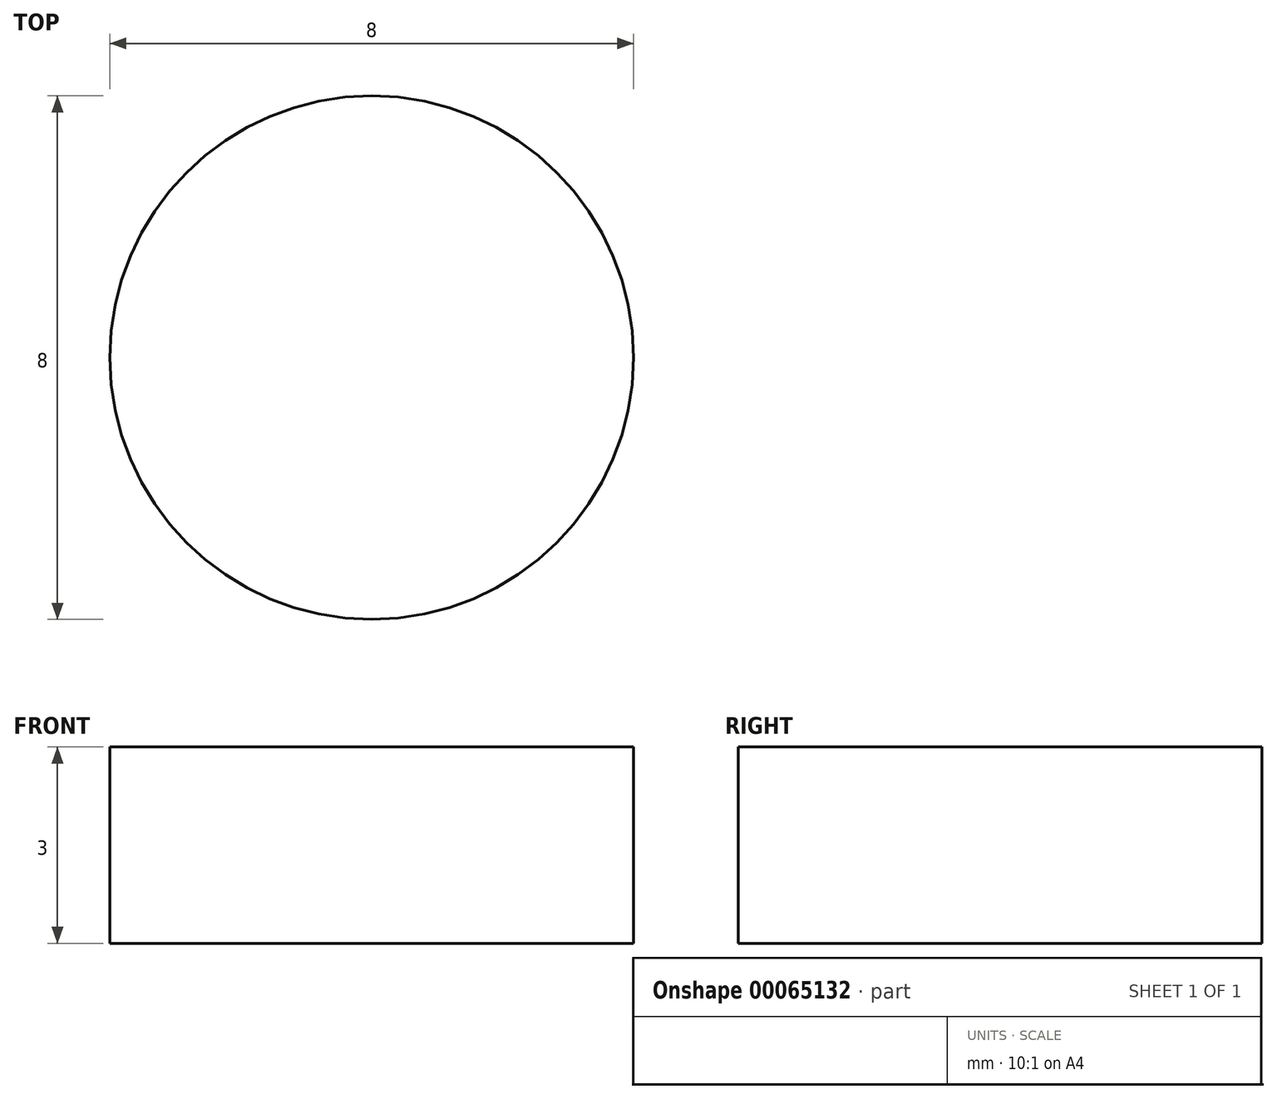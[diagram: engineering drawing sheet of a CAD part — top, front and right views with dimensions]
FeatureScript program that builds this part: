
annotation { "Feature Type Name" : "Feature", "Feature Type Description" : "" }
export const myFeature = defineFeature(function(context is Context, id is Id, definition is map)
    precondition{}
    {
        {
            var Q0;
            Q0=qCreatedBy(makeId("Top.planeOp"),FACE);
            var sketch = newSketch(context, id + "F0", { "sketchPlane" : qUnion([Q0])});
            skCircle(sketch, "E0", {"center": v(0, 0) * mm, "radius": 4 * mm});
            skSolve(sketch);
        }
        {
            var Q0;
            Q0 = qSketchRegion(id + "F0", true);
            extrude(context, id + "F1", {"entities" : qUnion([Q0]), "depth" : 3 * mm});
        }
    });
